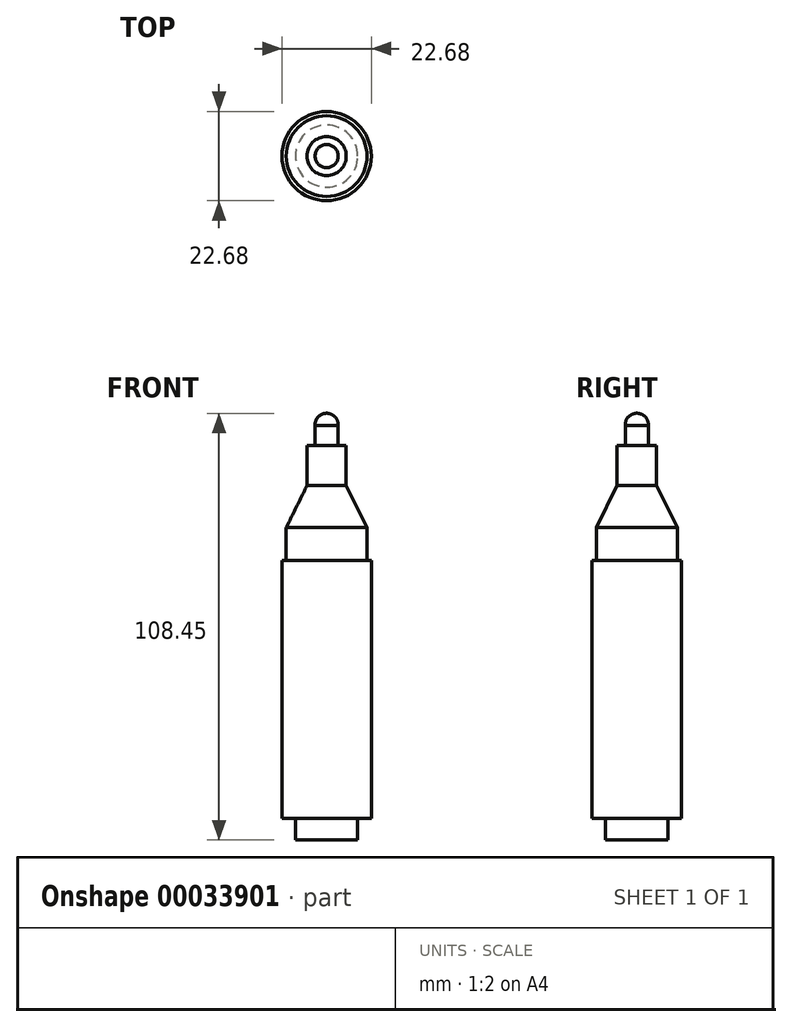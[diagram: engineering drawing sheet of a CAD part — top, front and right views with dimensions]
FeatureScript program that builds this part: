
annotation { "Feature Type Name" : "Feature", "Feature Type Description" : "" }
export const myFeature = defineFeature(function(context is Context, id is Id, definition is map)
    precondition{}
    {
        {
            var Q0;
            Q0=qCreatedBy(makeId("Front.planeOp"),FACE);
            var sketch = newSketch(context, id + "F0", { "sketchPlane" : qUnion([Q0])});
            skLineSegment(sketch, "E0", {"start": v(0, 0) * mm, "end": v(0, 114.06) * mm});
            skArc(sketch, "E1", {"start": v(0, 108.45) * mm, "mid": v(-2.13, 107.54) * mm, "end": v(-2.94, 105.38) * mm});
            skLineSegment(sketch, "E2", {"start": v(-2.94, 105.38) * mm, "end": v(-2.94, 100.3) * mm});
            skLineSegment(sketch, "E3", {"start": v(-2.94, 100.3) * mm, "end": v(-4.98, 100.3) * mm});
            skLineSegment(sketch, "E4", {"start": v(-4.98, 100.3) * mm, "end": v(-4.98, 90.1) * mm});
            skLineSegment(sketch, "E5", {"start": v(-4.98, 90.1) * mm, "end": v(-10.27, 79.4) * mm});
            skLineSegment(sketch, "E6", {"start": v(-10.27, 79.4) * mm, "end": v(-10.27, 71.05) * mm});
            skLineSegment(sketch, "E7", {"start": v(-10.27, 71.05) * mm, "end": v(-11.34, 71.05) * mm});
            skLineSegment(sketch, "E8", {"start": v(-11.34, 71.05) * mm, "end": v(-11.34, 5.52) * mm});
            skLineSegment(sketch, "E9", {"start": v(-11.34, 5.52) * mm, "end": v(-7.9, 5.52) * mm});
            skLineSegment(sketch, "E10", {"start": v(-7.9, 5.52) * mm, "end": v(-7.9, 0) * mm});
            skLineSegment(sketch, "E11", {"start": v(-7.9, 0) * mm, "end": v(0, 0) * mm});
            skSolve(sketch);
        }
        {
            var Q0;
            {var subQ1=sQuery(id+"F0.wireOp",EDGE,"E1");Q0=makeQuery(id+"F0.imprint","IMPRINT",FACE,{"disambiguationData":[TD([[makeQuery(id+"F0.imprint","IMPRINT",EDGE,{"derivedFrom":subQ1}),1.0]])]});}
            var Q1;
            Q1=sQuery(id+"F0.wireOp",EDGE,"E0");
            revolve(context, id + "F1", {"entities" : qUnion([Q0]), "axis" : qUnion([Q1]), "revolveType" : RevolveType.FULL});
        }
    });
